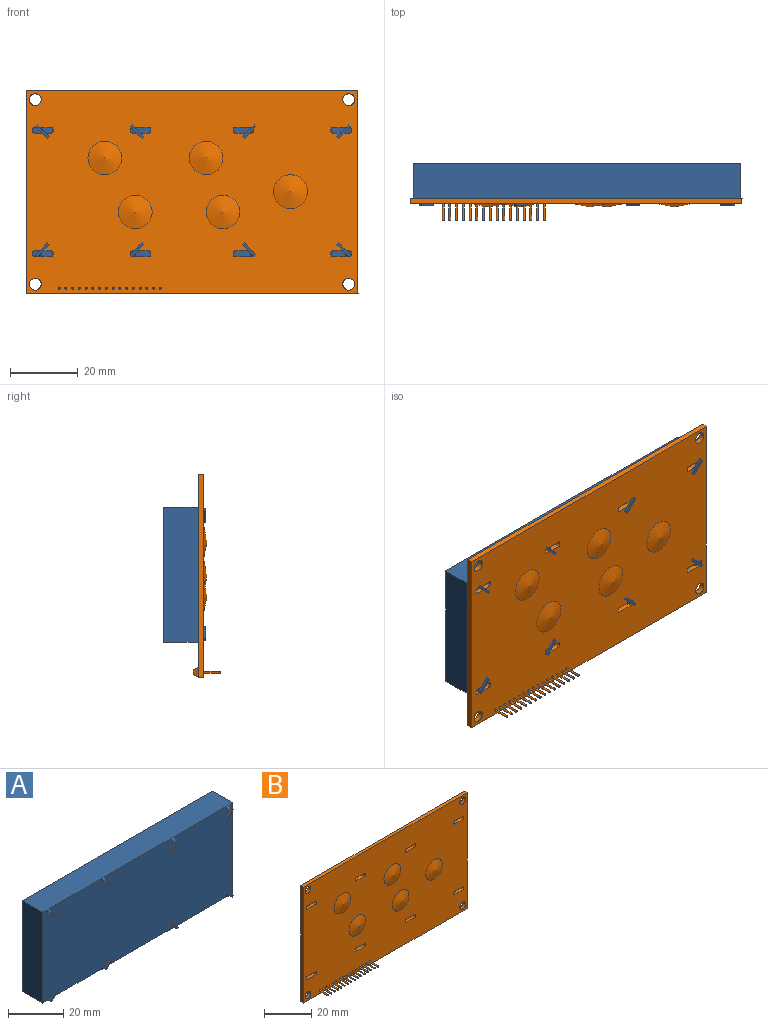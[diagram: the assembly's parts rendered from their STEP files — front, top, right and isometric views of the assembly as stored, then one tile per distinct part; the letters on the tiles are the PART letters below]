
ASSEMBLY  parts=2 mates=1
PART A: 109 faces, bbox 97x12.6x40 mm
  f0: plane 97x40mm, normal (0,-1,0), area 3871.6mm2, adj f2,f3,f4,f5,f29,f31,f32,f39
  f1: plane 97x40mm, normal (0,1,0), area 1627.1mm2, adj f2,f3,f4,f5,f6,f7,f8,f9
  f2: plane 40x10.3mm, normal (-1,0,0), area 412mm2, adj f0,f1,f3,f5
  f3: plane 97x10.3mm, normal (0,0,1), area 999.1mm2, adj f0,f1,f2,f4,f30,f40,f50,f54
  f4: plane 40x10.3mm, normal (1,0,0), area 412mm2, adj f0,f1,f3,f5
  f5: plane 97x10.3mm, normal (0,0,-1), area 999.1mm2, adj f0,f1,f2,f4,f70,f74,f90,f94
  f6: plane 26.8x1mm, normal (1,0,0), area 26.8mm2, adj f1,f7,f9,f28
  f7: plane 76.4x1mm, normal (0,0,-1), area 76.4mm2, adj f1,f6,f8,f28
  f8: plane 26.8x1mm, normal (-1,0,0), area 26.8mm2, adj f1,f7,f9,f28
  f9: plane 76.4x1mm, normal (0,0,1), area 76.4mm2, adj f1,f6,f8,f28
  f10: cylinder r=0.38mm len=0.8mm, axis (0,-1,0), area 0.9mm2, adj f11,f13,f22,f27
  f11: plane 88.4x0.8mm, normal (0,0,-1), area 70.7mm2, adj f10,f12,f23,f27
  f12: cylinder r=0.38mm len=0.8mm, axis (0,-1,0), area 0.9mm2, adj f11,f13,f25,f27
  f13: plane 88.4x0.8mm, normal (0,0,1), area 70.7mm2, adj f10,f12,f24,f27
  f14: cylinder r=0.38mm len=0.8mm, axis (0,-1,0), area 0.9mm2, adj f15,f17,f18,f26
  f15: plane 88.4x0.8mm, normal (0,0,-1), area 70.7mm2, adj f14,f16,f19,f26
  f16: cylinder r=0.38mm len=0.8mm, axis (0,-1,0), area 0.9mm2, adj f15,f17,f21,f26
  f17: plane 88.4x0.8mm, normal (0,0,1), area 70.7mm2, adj f14,f16,f20,f26
  f18: torus R=0.57mm, axis (0,-1,0), area 0.4mm2, adj f1,f14,f19,f20
  f19: cylinder r=0.2mm len=88.4mm, axis (-1,0,0), area 27.8mm2, adj f1,f15,f18,f21
  f20: cylinder r=0.2mm len=88.4mm, axis (1,0,0), area 27.8mm2, adj f1,f17,f18,f21
  f21: torus R=0.57mm, axis (0,-1,0), area 0.4mm2, adj f1,f16,f19,f20
  f22: torus R=0.57mm, axis (0,-1,0), area 0.4mm2, adj f1,f10,f23,f24
  f23: cylinder r=0.2mm len=88.4mm, axis (-1,0,0), area 27.8mm2, adj f1,f11,f22,f25
  f24: cylinder r=0.2mm len=88.4mm, axis (1,0,0), area 27.8mm2, adj f1,f13,f22,f25
  f25: torus R=0.57mm, axis (0,-1,0), area 0.4mm2, adj f1,f12,f23,f24
  f26: plane 89.15x0.75mm, normal (0,1,0), area 66.7mm2, adj f14,f15,f16,f17
  f27: plane 89.15x0.75mm, normal (0,1,0), area 66.7mm2, adj f10,f11,f12,f13
  f28: plane 76.4x26.8mm, normal (0,1,0), area 2047.5mm2, adj f6,f7,f8,f9
  f29: bspline ~2.12x1.4mm, area 1mm2, adj f0,f30,f31,f33
  f30: bspline ~1.59x1.5mm, area 2.4mm2, adj f3,f29,f32,f37
  f31: bspline ~1.63x1.42mm, area 2.4mm2, adj f0,f29,f32,f36
  f32: bspline ~1.4x1.06mm, area 1mm2, adj f0,f30,f31,f35
  f33: plane 3.01x3.01mm, normal (0,1,0), area 2.6mm2, adj f29,f36,f37,f38
  f34: plane 4.07x4.07mm, normal (0,-1,0), area 3.8mm2, adj f35,f36,f37,f38
  f35: plane 0.85x0.53mm, normal (-0.71,0,0.71), area 0.6mm2, adj f32,f34,f36,f37
  f36: plane 3.54x3.54mm, normal (-0.71,0,-0.71), area 4.3mm2, adj f31,f33,f34,f35,f38
  f37: plane 3.54x3.54mm, normal (0.71,0,0.71), area 4.3mm2, adj f30,f33,f34,f35,f38
  f38: plane 0.85x0.53mm, normal (0.71,0,-0.71), area 0.6mm2, adj f33,f34,f36,f37
  f39: bspline ~2.12x1.4mm, area 1mm2, adj f0,f40,f41,f43
  f40: bspline ~1.59x1.5mm, area 2.4mm2, adj f3,f39,f42,f47
  f41: bspline ~1.63x1.42mm, area 2.4mm2, adj f0,f39,f42,f46
  f42: bspline ~1.4x1.06mm, area 1mm2, adj f0,f40,f41,f45
  f43: plane 3.01x3.01mm, normal (0,1,0), area 2.6mm2, adj f39,f46,f47,f48
  f44: plane 4.07x4.07mm, normal (0,-1,0), area 3.8mm2, adj f45,f46,f47,f48
  f45: plane 0.85x0.53mm, normal (-0.71,0,0.71), area 0.6mm2, adj f42,f44,f46,f47
  f46: plane 3.54x3.54mm, normal (-0.71,0,-0.71), area 4.3mm2, adj f41,f43,f44,f45,f48
  f47: plane 3.54x3.54mm, normal (0.71,0,0.71), area 4.3mm2, adj f40,f43,f44,f45,f48
  f48: plane 0.85x0.53mm, normal (0.71,0,-0.71), area 0.6mm2, adj f43,f44,f46,f47
  f49: bspline ~2.12x1.4mm, area 1mm2, adj f0,f50,f51,f57
  f50: bspline ~1.59x1.5mm, area 2.4mm2, adj f3,f49,f52,f61
  f51: bspline ~1.63x1.42mm, area 2.4mm2, adj f0,f49,f52,f60
  f52: bspline ~1.4x1.06mm, area 1mm2, adj f0,f50,f51,f59
  f53: bspline ~2.12x1.4mm, area 1mm2, adj f0,f54,f55,f63
  f54: bspline ~1.59x1.5mm, area 2.4mm2, adj f3,f53,f56,f67
  f55: bspline ~1.63x1.42mm, area 2.4mm2, adj f0,f53,f56,f66
  f56: bspline ~1.4x1.06mm, area 1mm2, adj f0,f54,f55,f65
  f57: plane 3.01x3.01mm, normal (0,1,0), area 2.6mm2, adj f49,f60,f61,f62
  f58: plane 4.07x4.07mm, normal (0,-1,0), area 3.8mm2, adj f59,f60,f61,f62
  f59: plane 0.85x0.53mm, normal (0.71,0,0.71), area 0.6mm2, adj f52,f58,f60,f61
  f60: plane 3.54x3.54mm, normal (0.71,0,-0.71), area 4.3mm2, adj f51,f57,f58,f59,f62
  f61: plane 3.54x3.54mm, normal (-0.71,0,0.71), area 4.3mm2, adj f50,f57,f58,f59,f62
  f62: plane 0.85x0.53mm, normal (-0.71,0,-0.71), area 0.6mm2, adj f57,f58,f60,f61
  f63: plane 3.01x3.01mm, normal (0,1,0), area 2.6mm2, adj f53,f66,f67,f68
  f64: plane 4.07x4.07mm, normal (0,-1,0), area 3.8mm2, adj f65,f66,f67,f68
  f65: plane 0.85x0.53mm, normal (0.71,0,0.71), area 0.6mm2, adj f56,f64,f66,f67
  f66: plane 3.54x3.54mm, normal (0.71,0,-0.71), area 4.3mm2, adj f55,f63,f64,f65,f68
  f67: plane 3.54x3.54mm, normal (-0.71,0,0.71), area 4.3mm2, adj f54,f63,f64,f65,f68
  f68: plane 0.85x0.53mm, normal (-0.71,0,-0.71), area 0.6mm2, adj f63,f64,f66,f67
  f69: bspline ~2.12x1.4mm, area 1mm2, adj f0,f70,f71,f77
  f70: bspline ~1.59x1.5mm, area 2.4mm2, adj f5,f69,f72,f81
  f71: bspline ~1.63x1.42mm, area 2.4mm2, adj f0,f69,f72,f80
  f72: bspline ~1.4x1.06mm, area 1mm2, adj f0,f70,f71,f79
  f73: bspline ~2.12x1.4mm, area 1mm2, adj f0,f74,f75,f83
  f74: bspline ~1.59x1.5mm, area 2.4mm2, adj f5,f73,f76,f87
  f75: bspline ~1.63x1.42mm, area 2.4mm2, adj f0,f73,f76,f86
  f76: bspline ~1.4x1.06mm, area 1mm2, adj f0,f74,f75,f85
  f77: plane 3.01x3.01mm, normal (0,1,0), area 2.6mm2, adj f69,f80,f81,f82
  f78: plane 4.07x4.07mm, normal (0,-1,0), area 3.7mm2, adj f79,f80,f81,f82
  f79: plane 0.85x0.53mm, normal (0.71,0,-0.71), area 0.6mm2, adj f72,f78,f80,f81
  f80: plane 3.54x3.54mm, normal (0.71,0,0.71), area 4.3mm2, adj f71,f77,f78,f79,f82
  f81: plane 3.54x3.54mm, normal (-0.71,0,-0.71), area 4.3mm2, adj f70,f77,f78,f79,f82
  f82: plane 0.85x0.53mm, normal (-0.71,0,0.71), area 0.6mm2, adj f77,f78,f80,f81
  f83: plane 3.01x3.01mm, normal (0,1,0), area 2.6mm2, adj f73,f86,f87,f88
  f84: plane 4.07x4.07mm, normal (0,-1,0), area 3.7mm2, adj f85,f86,f87,f88
  f85: plane 0.85x0.53mm, normal (0.71,0,-0.71), area 0.6mm2, adj f76,f84,f86,f87
  f86: plane 3.54x3.54mm, normal (0.71,0,0.71), area 4.3mm2, adj f75,f83,f84,f85,f88
  f87: plane 3.54x3.54mm, normal (-0.71,0,-0.71), area 4.3mm2, adj f74,f83,f84,f85,f88
  f88: plane 0.85x0.53mm, normal (-0.71,0,0.71), area 0.6mm2, adj f83,f84,f86,f87
  f89: bspline ~2.12x1.4mm, area 1mm2, adj f0,f90,f91,f97
  f90: bspline ~1.59x1.5mm, area 2.4mm2, adj f5,f89,f92,f101
  f91: bspline ~1.63x1.42mm, area 2.4mm2, adj f0,f89,f92,f100
  f92: bspline ~1.4x1.06mm, area 1mm2, adj f0,f90,f91,f99
  f93: bspline ~2.12x1.4mm, area 1mm2, adj f0,f94,f95,f103
  f94: bspline ~1.59x1.5mm, area 2.4mm2, adj f5,f93,f96,f107
  f95: bspline ~1.63x1.42mm, area 2.4mm2, adj f0,f93,f96,f106
  f96: bspline ~1.4x1.06mm, area 1mm2, adj f0,f94,f95,f105
  f97: plane 3.01x3.01mm, normal (0,1,0), area 2.6mm2, adj f89,f100,f101,f102
  f98: plane 4.07x4.07mm, normal (0,-1,0), area 3.7mm2, adj f99,f100,f101,f102
  f99: plane 0.85x0.53mm, normal (-0.71,0,-0.71), area 0.6mm2, adj f92,f98,f100,f101
  f100: plane 3.54x3.54mm, normal (-0.71,0,0.71), area 4.3mm2, adj f91,f97,f98,f99,f102
  f101: plane 3.54x3.54mm, normal (0.71,0,-0.71), area 4.3mm2, adj f90,f97,f98,f99,f102
  f102: plane 0.85x0.53mm, normal (0.71,0,0.71), area 0.6mm2, adj f97,f98,f100,f101
  f103: plane 3.01x3.01mm, normal (0,1,0), area 2.6mm2, adj f93,f106,f107,f108
  f104: plane 4.07x4.07mm, normal (0,-1,0), area 3.7mm2, adj f105,f106,f107,f108
  f105: plane 0.85x0.53mm, normal (-0.71,0,-0.71), area 0.6mm2, adj f96,f104,f106,f107
  f106: plane 3.54x3.54mm, normal (-0.71,0,0.71), area 4.3mm2, adj f95,f103,f104,f105,f108
  f107: plane 3.54x3.54mm, normal (0.71,0,-0.71), area 4.3mm2, adj f94,f103,f104,f105,f108
  f108: plane 0.85x0.53mm, normal (0.71,0,0.71), area 0.6mm2, adj f103,f104,f106,f107
PART B: 175 faces, bbox 98.4x8.1x60.2 mm
  f0: plane 98.35x60.15mm, normal (0,1,0), area 5725.4mm2, adj f1,f2,f3,f4,f5,f6,f7,f8
  f1: plane 98.35x1.6mm, normal (0,0,1), area 157.4mm2, adj f0,f2,f61,f73
  f2: plane 60.15x1.6mm, normal (1,0,0), area 96.2mm2, adj f0,f1,f3,f73
  f3: plane 98.35x1.6mm, normal (0,0,-1), area 157.4mm2, adj f0,f2,f61,f73
  f4: cylinder r=0.5mm len=1.6mm, axis (0,-1,0), area 1.3mm2, adj f0,f5,f64,f73
  f5: plane 5x1.6mm, normal (0,0,1), area 8mm2, adj f0,f4,f6,f73
  f6: cylinder r=0.5mm len=1.6mm, axis (0,-1,0), area 1.3mm2, adj f0,f5,f7,f73
  f7: plane 1.6x0.6mm, normal (-1,0,0), area 1mm2, adj f0,f6,f8,f73
  f8: cylinder r=0.5mm len=1.6mm, axis (0,-1,0), area 1.3mm2, adj f0,f7,f9,f73
  f9: plane 5x1.6mm, normal (0,0,-1), area 8mm2, adj f0,f8,f10,f73
  f10: cylinder r=0.5mm len=1.6mm, axis (0,-1,0), area 1.3mm2, adj f0,f9,f64,f73
  f11: cylinder r=0.5mm len=1.6mm, axis (0,-1,0), area 1.3mm2, adj f0,f12,f65,f73
  f12: plane 5x1.6mm, normal (0,0,1), area 8mm2, adj f0,f11,f13,f73
  f13: cylinder r=0.5mm len=1.6mm, axis (0,-1,0), area 1.3mm2, adj f0,f12,f14,f73
  f14: plane 1.6x0.6mm, normal (-1,0,0), area 1mm2, adj f0,f13,f15,f73
  f15: cylinder r=0.5mm len=1.6mm, axis (0,-1,0), area 1.3mm2, adj f0,f14,f16,f73
  f16: plane 5x1.6mm, normal (0,0,-1), area 8mm2, adj f0,f15,f17,f73
  f17: cylinder r=0.5mm len=1.6mm, axis (0,-1,0), area 1.3mm2, adj f0,f16,f65,f73
  f18: cylinder r=0.5mm len=1.6mm, axis (0,-1,0), area 1.3mm2, adj f0,f19,f66,f73
  f19: plane 5x1.6mm, normal (0,0,1), area 8mm2, adj f0,f18,f20,f73
  f20: cylinder r=0.5mm len=1.6mm, axis (0,-1,0), area 1.3mm2, adj f0,f19,f21,f73
  f21: plane 1.6x0.6mm, normal (-1,0,0), area 1mm2, adj f0,f20,f22,f73
  f22: cylinder r=0.5mm len=1.6mm, axis (0,-1,0), area 1.3mm2, adj f0,f21,f23,f73
  f23: plane 5x1.6mm, normal (0,0,-1), area 8mm2, adj f0,f22,f24,f73
  f24: cylinder r=0.5mm len=1.6mm, axis (0,-1,0), area 1.3mm2, adj f0,f23,f66,f73
  f25: cylinder r=0.5mm len=1.6mm, axis (0,-1,0), area 1.3mm2, adj f0,f26,f67,f73
  f26: plane 5x1.6mm, normal (0,0,1), area 8mm2, adj f0,f25,f27,f73
  f27: cylinder r=0.5mm len=1.6mm, axis (0,-1,0), area 1.3mm2, adj f0,f26,f28,f73
  f28: plane 1.6x0.6mm, normal (-1,0,0), area 1mm2, adj f0,f27,f29,f73
  f29: cylinder r=0.5mm len=1.6mm, axis (0,-1,0), area 1.3mm2, adj f0,f28,f30,f73
  f30: plane 5x1.6mm, normal (0,0,-1), area 8mm2, adj f0,f29,f31,f73
  f31: cylinder r=0.5mm len=1.6mm, axis (0,-1,0), area 1.3mm2, adj f0,f30,f67,f73
  f32: cylinder r=0.5mm len=1.6mm, axis (0,-1,0), area 1.3mm2, adj f0,f33,f68,f73
  f33: plane 5x1.6mm, normal (0,0,-1), area 8mm2, adj f0,f32,f34,f73
  f34: cylinder r=0.5mm len=1.6mm, axis (0,-1,0), area 1.3mm2, adj f0,f33,f35,f73
  f35: plane 1.6x0.6mm, normal (1,0,0), area 1mm2, adj f0,f34,f36,f73
  f36: cylinder r=0.5mm len=1.6mm, axis (0,-1,0), area 1.3mm2, adj f0,f35,f37,f73
  f37: plane 5x1.6mm, normal (0,0,1), area 8mm2, adj f0,f36,f38,f73
  f38: cylinder r=0.5mm len=1.6mm, axis (0,-1,0), area 1.3mm2, adj f0,f37,f68,f73
  f39: cylinder r=0.5mm len=1.6mm, axis (0,-1,0), area 1.3mm2, adj f0,f40,f69,f73
  f40: plane 5x1.6mm, normal (0,0,-1), area 8mm2, adj f0,f39,f41,f73
  f41: cylinder r=0.5mm len=1.6mm, axis (0,-1,0), area 1.3mm2, adj f0,f40,f42,f73
  f42: plane 1.6x0.6mm, normal (1,0,0), area 1mm2, adj f0,f41,f43,f73
  f43: cylinder r=0.5mm len=1.6mm, axis (0,-1,0), area 1.3mm2, adj f0,f42,f44,f73
  f44: plane 5x1.6mm, normal (0,0,1), area 8mm2, adj f0,f43,f45,f73
  f45: cylinder r=0.5mm len=1.6mm, axis (0,-1,0), area 1.3mm2, adj f0,f44,f69,f73
  f46: cylinder r=0.5mm len=1.6mm, axis (0,-1,0), area 1.3mm2, adj f0,f47,f70,f73
  f47: plane 5x1.6mm, normal (0,0,-1), area 8mm2, adj f0,f46,f48,f73
  f48: cylinder r=0.5mm len=1.6mm, axis (0,-1,0), area 1.3mm2, adj f0,f47,f49,f73
  f49: plane 1.6x0.6mm, normal (1,0,0), area 1mm2, adj f0,f48,f50,f73
  f50: cylinder r=0.5mm len=1.6mm, axis (0,-1,0), area 1.3mm2, adj f0,f49,f51,f73
  f51: plane 5x1.6mm, normal (0,0,1), area 8mm2, adj f0,f50,f52,f73
  f52: cylinder r=0.5mm len=1.6mm, axis (0,-1,0), area 1.3mm2, adj f0,f51,f70,f73
  f53: cylinder r=0.5mm len=1.6mm, axis (0,-1,0), area 1.3mm2, adj f0,f54,f71,f73
  f54: plane 5x1.6mm, normal (0,0,-1), area 8mm2, adj f0,f53,f55,f73
  f55: cylinder r=0.5mm len=1.6mm, axis (0,-1,0), area 1.3mm2, adj f0,f54,f56,f73
  f56: plane 1.6x0.6mm, normal (1,0,0), area 1mm2, adj f0,f55,f57,f73
  f57: cylinder r=0.5mm len=1.6mm, axis (0,-1,0), area 1.3mm2, adj f0,f56,f58,f73
  f58: plane 5x1.6mm, normal (0,0,1), area 8mm2, adj f0,f57,f59,f73
  f59: cylinder r=0.5mm len=1.6mm, axis (0,-1,0), area 1.3mm2, adj f0,f58,f71,f73
  f60: cylinder r=1.75mm len=3.5mm, axis (0,-1,0), area 17.6mm2, adj f0,f73
  f61: plane 60.15x1.6mm, normal (-1,0,0), area 96.2mm2, adj f0,f1,f3,f73
  f62: cylinder r=1.75mm len=3.5mm, axis (0,-1,0), area 17.6mm2, adj f0,f73
  f63: cylinder r=1.75mm len=3.5mm, axis (0,-1,0), area 17.6mm2, adj f0,f73
  f64: plane 1.6x0.6mm, normal (1,0,0), area 1mm2, adj f0,f4,f10,f73
  f65: plane 1.6x0.6mm, normal (1,0,0), area 1mm2, adj f0,f11,f17,f73
  f66: plane 1.6x0.6mm, normal (1,0,0), area 1mm2, adj f0,f18,f24,f73
  f67: plane 1.6x0.6mm, normal (1,0,0), area 1mm2, adj f0,f25,f31,f73
  f68: plane 1.6x0.6mm, normal (-1,0,0), area 1mm2, adj f0,f32,f38,f73
  f69: plane 1.6x0.6mm, normal (-1,0,0), area 1mm2, adj f0,f39,f45,f73
  f70: plane 1.6x0.6mm, normal (-1,0,0), area 1mm2, adj f0,f46,f52,f73
  f71: plane 1.6x0.6mm, normal (-1,0,0), area 1mm2, adj f0,f53,f59,f73
  f72: cylinder r=1.75mm len=3.5mm, axis (0,-1,0), area 17.6mm2, adj f0,f73
  f73: plane 98.35x60.15mm, normal (0,-1,0), area 5405mm2, adj f1,f2,f3,f4,f5,f6,f7,f8
  f74: plane 1.6x1.5mm, normal (0,0.47,-0.88), area 1.4mm2, adj f0,f75,f77
  f75: plane 3x1.5mm, normal (-0.88,0.47,0), area 3.7mm2, adj f0,f74,f76,f77
  f76: plane 1.6x1.5mm, normal (0,0.47,0.88), area 1.4mm2, adj f0,f75,f77
  f77: plane 3x1.5mm, normal (0.88,0.47,0), area 3.7mm2, adj f0,f74,f75,f76
  f78: plane 1.6x1.5mm, normal (0,0.47,-0.88), area 1.4mm2, adj f0,f79,f81
  f79: plane 3x1.5mm, normal (-0.88,0.47,0), area 3.7mm2, adj f0,f78,f80,f81
  f80: plane 1.6x1.5mm, normal (0,0.47,0.88), area 1.4mm2, adj f0,f79,f81
  f81: plane 3x1.5mm, normal (0.88,0.47,0), area 3.7mm2, adj f0,f78,f79,f80
  f82: plane 1.6x1.5mm, normal (0,0.47,-0.88), area 1.4mm2, adj f0,f83,f85
  f83: plane 3x1.5mm, normal (-0.88,0.47,0), area 3.7mm2, adj f0,f82,f84,f85
  f84: plane 1.6x1.5mm, normal (0,0.47,0.88), area 1.4mm2, adj f0,f83,f85
  f85: plane 3x1.5mm, normal (0.88,0.47,0), area 3.7mm2, adj f0,f82,f83,f84
  f86: plane 1.6x1.5mm, normal (0,0.47,-0.88), area 1.4mm2, adj f0,f87,f89
  f87: plane 3x1.5mm, normal (-0.88,0.47,0), area 3.7mm2, adj f0,f86,f88,f89
  f88: plane 1.6x1.5mm, normal (0,0.47,0.88), area 1.4mm2, adj f0,f87,f89
  f89: plane 3x1.5mm, normal (0.88,0.47,0), area 3.7mm2, adj f0,f86,f87,f88
  f90: plane 1.6x1.5mm, normal (0,0.47,0.88), area 1.4mm2, adj f0,f91,f93
  f91: plane 3x1.5mm, normal (0.88,0.47,0), area 3.7mm2, adj f0,f90,f92,f93
  f92: plane 1.6x1.5mm, normal (0,0.47,-0.88), area 1.4mm2, adj f0,f91,f93
  f93: plane 3x1.5mm, normal (-0.88,0.47,0), area 3.7mm2, adj f0,f90,f91,f92
  f94: plane 1.6x1.5mm, normal (0,0.47,-0.88), area 1.4mm2, adj f0,f95,f97
  f95: plane 3x1.5mm, normal (-0.88,0.47,0), area 3.7mm2, adj f0,f94,f96,f97
  f96: plane 1.6x1.5mm, normal (0,0.47,0.88), area 1.4mm2, adj f0,f95,f97
  f97: plane 3x1.5mm, normal (0.88,0.47,0), area 3.7mm2, adj f0,f94,f95,f96
  f98: plane 1.6x1.5mm, normal (0,0.47,-0.88), area 1.4mm2, adj f0,f99,f101
  f99: plane 3x1.5mm, normal (-0.88,0.47,0), area 3.7mm2, adj f0,f98,f100,f101
  f100: plane 1.6x1.5mm, normal (0,0.47,0.88), area 1.4mm2, adj f0,f99,f101
  f101: plane 3x1.5mm, normal (0.88,0.47,0), area 3.7mm2, adj f0,f98,f99,f100
  f102: plane 1.6x1.5mm, normal (0,0.47,-0.88), area 1.4mm2, adj f0,f103,f105
  f103: plane 3x1.5mm, normal (-0.88,0.47,0), area 3.7mm2, adj f0,f102,f104,f105
  f104: plane 1.6x1.5mm, normal (0,0.47,0.88), area 1.4mm2, adj f0,f103,f105
  f105: plane 3x1.5mm, normal (0.88,0.47,0), area 3.7mm2, adj f0,f102,f103,f104
  f106: plane 1.6x1.5mm, normal (0,0.47,0.88), area 1.4mm2, adj f0,f107,f109
  f107: plane 3x1.5mm, normal (0.88,0.47,0), area 3.7mm2, adj f0,f106,f108,f109
  f108: plane 1.6x1.5mm, normal (0,0.47,-0.88), area 1.4mm2, adj f0,f107,f109
  f109: plane 3x1.5mm, normal (-0.88,0.47,0), area 3.7mm2, adj f0,f106,f107,f108
  f110: plane 1.6x1.5mm, normal (0,0.47,-0.88), area 1.4mm2, adj f0,f111,f113
  f111: plane 3x1.5mm, normal (-0.88,0.47,0), area 3.7mm2, adj f0,f110,f112,f113
  f112: plane 1.6x1.5mm, normal (0,0.47,0.88), area 1.4mm2, adj f0,f111,f113
  f113: plane 3x1.5mm, normal (0.88,0.47,0), area 3.7mm2, adj f0,f110,f111,f112
  f114: plane 1.6x1.5mm, normal (0,0.47,-0.88), area 1.4mm2, adj f0,f115,f117
  f115: plane 3x1.5mm, normal (-0.88,0.47,0), area 3.7mm2, adj f0,f114,f116,f117
  f116: plane 1.6x1.5mm, normal (0,0.47,0.88), area 1.4mm2, adj f0,f115,f117
  f117: plane 3x1.5mm, normal (0.88,0.47,0), area 3.7mm2, adj f0,f114,f115,f116
  f118: plane 1.6x1.5mm, normal (0,0.47,-0.88), area 1.4mm2, adj f0,f119,f121
  f119: plane 3x1.5mm, normal (-0.88,0.47,0), area 3.7mm2, adj f0,f118,f120,f121
  f120: plane 1.6x1.5mm, normal (0,0.47,0.88), area 1.4mm2, adj f0,f119,f121
  f121: plane 3x1.5mm, normal (0.88,0.47,0), area 3.7mm2, adj f0,f118,f119,f120
  f122: plane 1.6x1.5mm, normal (0,0.47,0.88), area 1.4mm2, adj f0,f123,f125
  f123: plane 3x1.5mm, normal (0.88,0.47,0), area 3.7mm2, adj f0,f122,f124,f125
  f124: plane 1.6x1.5mm, normal (0,0.47,-0.88), area 1.4mm2, adj f0,f123,f125
  f125: plane 3x1.5mm, normal (-0.88,0.47,0), area 3.7mm2, adj f0,f122,f123,f124
  f126: plane 1.6x1.5mm, normal (0,0.47,-0.88), area 1.4mm2, adj f0,f127,f129
  f127: plane 3x1.5mm, normal (-0.88,0.47,0), area 3.7mm2, adj f0,f126,f128,f129
  f128: plane 1.6x1.5mm, normal (0,0.47,0.88), area 1.4mm2, adj f0,f127,f129
  f129: plane 3x1.5mm, normal (0.88,0.47,0), area 3.7mm2, adj f0,f126,f127,f128
  f130: plane 1.6x1.5mm, normal (0,0.47,-0.88), area 1.4mm2, adj f0,f131,f133
  f131: plane 3x1.5mm, normal (-0.88,0.47,0), area 3.7mm2, adj f0,f130,f132,f133
  f132: plane 1.6x1.5mm, normal (0,0.47,0.88), area 1.4mm2, adj f0,f131,f133
  f133: plane 3x1.5mm, normal (0.88,0.47,0), area 3.7mm2, adj f0,f130,f131,f132
  f134: plane 1.6x1.5mm, normal (0,0.47,-0.88), area 1.4mm2, adj f0,f135,f137
  f135: plane 3x1.5mm, normal (-0.88,0.47,0), area 3.7mm2, adj f0,f134,f136,f137
  f136: plane 1.6x1.5mm, normal (0,0.47,0.88), area 1.4mm2, adj f0,f135,f137
  f137: plane 3x1.5mm, normal (0.88,0.47,0), area 3.7mm2, adj f0,f134,f135,f136
  f138: cylinder r=0.3mm len=5mm, axis (0,1,0), area 9.4mm2, adj f73,f139
  f139: plane 0.6x0.6mm, normal (0,-1,0), area 0.3mm2, adj f138
  f140: cylinder r=0.3mm len=5mm, axis (0,1,0), area 9.4mm2, adj f73,f141
  f141: plane 0.6x0.6mm, normal (0,-1,0), area 0.3mm2, adj f140
  f142: cylinder r=0.3mm len=5mm, axis (0,1,0), area 9.4mm2, adj f73,f143
  f143: plane 0.6x0.6mm, normal (0,-1,0), area 0.3mm2, adj f142
  f144: cylinder r=0.3mm len=5mm, axis (0,1,0), area 9.4mm2, adj f73,f145
  f145: plane 0.6x0.6mm, normal (0,-1,0), area 0.3mm2, adj f144
  f146: cylinder r=0.3mm len=5mm, axis (0,1,0), area 9.4mm2, adj f73,f147
  f147: plane 0.6x0.6mm, normal (0,-1,0), area 0.3mm2, adj f146
  f148: cylinder r=0.3mm len=5mm, axis (0,1,0), area 9.4mm2, adj f73,f149
  f149: plane 0.6x0.6mm, normal (0,-1,0), area 0.3mm2, adj f148
  f150: cylinder r=0.3mm len=5mm, axis (0,1,0), area 9.4mm2, adj f73,f151
  f151: plane 0.6x0.6mm, normal (0,-1,0), area 0.3mm2, adj f150
  f152: cylinder r=0.3mm len=5mm, axis (0,1,0), area 9.4mm2, adj f73,f153
  f153: plane 0.6x0.6mm, normal (0,-1,0), area 0.3mm2, adj f152
  f154: cylinder r=0.3mm len=5mm, axis (0,1,0), area 9.4mm2, adj f73,f155
  f155: plane 0.6x0.6mm, normal (0,-1,0), area 0.3mm2, adj f154
  f156: cylinder r=0.3mm len=5mm, axis (0,1,0), area 9.4mm2, adj f73,f157
  f157: plane 0.6x0.6mm, normal (0,-1,0), area 0.3mm2, adj f156
  f158: cylinder r=0.3mm len=5mm, axis (0,1,0), area 9.4mm2, adj f73,f159
  f159: plane 0.6x0.6mm, normal (0,-1,0), area 0.3mm2, adj f158
  f160: cylinder r=0.3mm len=5mm, axis (0,1,0), area 9.4mm2, adj f73,f161
  f161: plane 0.6x0.6mm, normal (0,-1,0), area 0.3mm2, adj f160
  f162: cylinder r=0.3mm len=5mm, axis (0,1,0), area 9.4mm2, adj f73,f163
  f163: plane 0.6x0.6mm, normal (0,-1,0), area 0.3mm2, adj f162
  f164: cylinder r=0.3mm len=5mm, axis (0,1,0), area 9.4mm2, adj f73,f165
  f165: plane 0.6x0.6mm, normal (0,-1,0), area 0.3mm2, adj f164
  f166: cylinder r=0.3mm len=5mm, axis (0,1,0), area 9.4mm2, adj f73,f167
  f167: plane 0.6x0.6mm, normal (0,-1,0), area 0.3mm2, adj f166
  f168: cylinder r=0.3mm len=5mm, axis (0,1,0), area 9.4mm2, adj f73,f169
  f169: plane 0.6x0.6mm, normal (0,-1,0), area 0.3mm2, adj f168
  f170: cone r=5mm half-angle=79deg, axis (0,1,0), area 80mm2, adj f73
  f171: cone r=5mm half-angle=79deg, axis (0,1,0), area 80mm2, adj f73
  f172: cone r=5mm half-angle=79deg, axis (0,1,0), area 80mm2, adj f73
  f173: cone r=5mm half-angle=79deg, axis (0,1,0), area 80mm2, adj f73
  f174: cone r=5mm half-angle=79deg, axis (0,1,0), area 80mm2, adj f73
PLACE A rot(axis=(0.15,-0.48,-0.86),0deg) t=(-51.92,-1.58,78.32)mm
PLACE B rot(axis=(0.15,-0.48,-0.86),0deg) t=(-52.92,-12.48,88.01)mm
MATE fastened A.f0 <-> B.f0  axis (0,-1,0) through (-3.42,-10.88,58.32)mm
